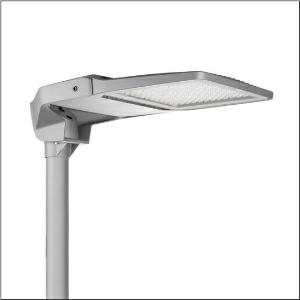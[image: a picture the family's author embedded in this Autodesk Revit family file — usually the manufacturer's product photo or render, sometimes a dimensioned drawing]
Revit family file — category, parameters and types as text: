
# Revit family: floodlight_fl_20_midi___pl52_5xa7682e1d4ac_8927
name_source: partatom
category: Lighting Fixtures
units: mm (PartAtom-declared; Revit-internal decimal feet)

## family parameters
Cut with Voids When Loaded = No
Host = Face
Light Source = No
Part Type = Normal
Room Calculation Point = No
Round Connector Dimension = Use Diameter
Shared = No

## types (1)
- --- (1 x LED 3000K / CRI = 80 (unbekannt), 21030 lm, 3000K)
    Apparent Load = 208 VA
    CIE Flux Codes = 27 59 98 100 100
    Color Rendering = 80
    Color Temperature = 3000K
    Default Elevation = 1800 mm
    Description = Floodlight FL 20 midi, floodlight, primary light control with lens, of plastic, primary optical cover: protective disc, of toughened safety glass, transparent, light distribution: PL52, light emission: direct distribution, primary light characteristic: asymmetric, installation type: side-entry, post-top, LED, High Power LED, rated luminous flux: 21.030lm, luminous efficacy: 101lm/W, light colour: 830, colour temperature: 3000K, control gear: ECG Plus, control: flexible luminous flux parameterisation, time-dependent luminous flux control, digital communication interface, overheat protection, power reduction, electronic power reduction, with terminal, 5-pole, max. 2.5mm², mains connection: 220..240V, AC, 50/60Hz, rated input power: 208W, LED unit, of diecast aluminium, powder-coated, Siteco® metallic grey (DB 702S), corrosivity category C5 mid according to DIN EN ISO 12944, please order mast flange separately, incl. 1x M20 cable gland for cable Ø 6.5..12mm, inclination adjustable: 0°, 3°, 8°, 15°, length: 862mm, width: 450mm, height: 176mm, housing frame, of diecast aluminium, powder-coated, Siteco® metallic grey (DB 702S), mast flange adapter, of diecast aluminium, powder-coated, Siteco® metallic grey (DB 702S), DALI, protection rating (complete): IP66, insulation class (complete): insulation class II (safety insulation), certification: CE, ENEC, VDE, protection symbol: D, permissible operating ambient temperature: -40..+40°C, permissible operating ambient temperature for outdoor applications: -40..+50°C, standard: DIN EN 12944, packaging unit: 1 piece

Light Distribution: PL52
    Height = 76 mm
    Lamp = 1 x LED 3000K / CRI >= 80 (unbekannt)
    Lamp Light Flux = 21030 lm
    Lamp count = 1
    Length = 862 mm
    Luminous efficacy = 101 lm/W
    Manufacturer = Siteco
    ModVariant = No
    Model = 5XA7682E1D4AC
    Number of Poles = 1
    OnlyDefault = Yes
    Power Factor = 1
    Product Name = Floodlight FL 20 midi | PL52
    Product group = floodlight | pylon top
    ProductGroupID = 6101
    Protection Class = Protection class II
    Protection Degree = IP 66
    RLX_Detail_Level = 1
    RLX_Emergency_Light_Flux = 0 lm
    RLX_Emergency_Type = 0
    RLX_Emergency_Type_DB = No
    RlxData = <blob elided: 118541 chars, md5=25cde7bc>
    Socket = socket
    Standby Power = 0 W
    System Light Flux = 21030 lm
    System Power = 208 W
    Type Comments = factory setting: luminous flux: 100 % | dim-lin: 254 | 484 mA
    Type Image = l_1005941.jpg
    URL = http://relux.com
    VarID = @adj_147643
    Voltage = 0 V
    Weight = 0.00 kg
    Width = 450 mm

## geometry (parser evidence)
native form markers: Blend x4, Sweep x13
no freeform markers — native parametric forms only
